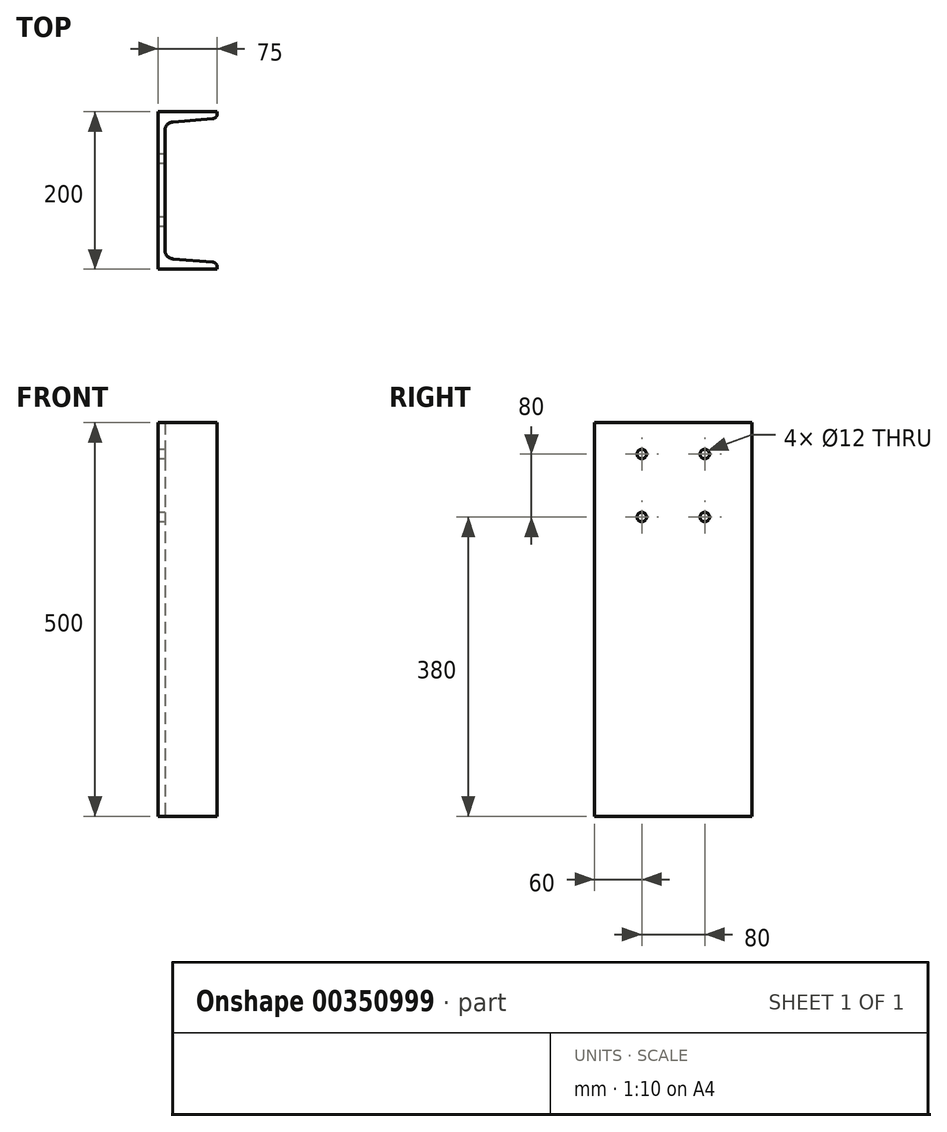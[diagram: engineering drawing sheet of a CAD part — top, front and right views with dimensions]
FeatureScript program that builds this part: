
annotation { "Feature Type Name" : "Feature", "Feature Type Description" : "" }
export const myFeature = defineFeature(function(context is Context, id is Id, definition is map)
    precondition{}
    {
        {
            var Q0;
            Q0=qCreatedBy(makeId("Top.planeOp"),FACE);
            var sketch = newSketch(context, id + "F0", { "sketchPlane" : qUnion([Q0])});
            skLineSegment(sketch, "E0", {"start": v(0, 0) * mm, "end": v(0, 100) * mm});
            skLineSegment(sketch, "E1", {"start": v(0, 0) * mm, "end": v(75, 0) * mm});
            skLineSegment(sketch, "E2.0", {"start": v(8.5, 24.44) * mm, "end": v(8.5, 100) * mm});
            skLineSegment(sketch, "E3", {"start": v(75, 0) * mm, "end": v(75, 2.5) * mm});
            skLineSegment(sketch, "E4", {"start": v(69.02, 8.98) * mm, "end": v(19.08, 12.97) * mm});
            skPoint(sketch, "E5.orphan", {"position": v(37.5, 11.5) * mm});
            skArc(sketch, "E6.filletArc", {"start": v(8.5, 24.44) * mm, "mid": v(11.55, 16.64) * mm, "end": v(19.08, 12.97) * mm});
            skPoint(sketch, "E7.visualSharp", {"position": v(75, 8.5) * mm});
            skArc(sketch, "E7.filletArc", {"start": v(75, 2.5) * mm, "mid": v(73.28, 6.9) * mm, "end": v(69.02, 8.98) * mm});
            skPoint(sketch, "E8.endSnap0", {"position": v(0, 100) * mm});
            skLineSegment(sketch, "E9.MirrorCS", {"start": v(75, 200) * mm, "end": v(75, 197.5) * mm});
            skArc(sketch, "E10.MirrorCS", {"start": v(75, 197.5) * mm, "mid": v(73.28, 193.1) * mm, "end": v(69.02, 191.02) * mm});
            skPoint(sketch, "E11.MirrorP", {"position": v(75, 191.5) * mm});
            skLineSegment(sketch, "E12.MirrorCS", {"start": v(69.02, 191.02) * mm, "end": v(19.08, 187.03) * mm});
            skLineSegment(sketch, "E13.MirrorCS", {"start": v(0, 200) * mm, "end": v(75, 200) * mm});
            skLineSegment(sketch, "E14.MirrorCS", {"start": v(8.5, 175.56) * mm, "end": v(8.5, 100) * mm});
            skArc(sketch, "E15.MirrorCS", {"start": v(8.5, 175.56) * mm, "mid": v(11.55, 183.36) * mm, "end": v(19.08, 187.03) * mm});
            skLineSegment(sketch, "E16.MirrorCS", {"start": v(0, 200) * mm, "end": v(0, 100) * mm});
            skPoint(sketch, "E17.MirrorP", {"position": v(37.5, 188.5) * mm});
            skSolve(sketch);
        }
        {
            var Q0;
            Q0=makeQuery(id+"F0.imprint","IMPRINT",FACE,{"disambiguationData":[TD([[makeQuery(id+"F0.imprint","IMPRINT",EDGE,{"derivedFrom":sQuery(id+"F0.wireOp",EDGE,"E0")}),-1.0]])]});
            extrude(context, id + "F1", {"entities" : qUnion([Q0]), "endBound" : BoundingType.SYMMETRIC, "depth" : 500 * mm});
        }
        {
            var Q0;
            Q0=makeQuery(id+"F1.opExtrude","SWEPT_FACE",FACE,{"disambiguationData":[OSD([sQuery(id+"F0.wireOp",EDGE,"E0"),sQuery(id+"F0.wireOp",EDGE,"E16.MirrorCS")])]});
            var sketch = newSketch(context, id + "F2", { "sketchPlane" : qUnion([Q0])});
            skLineSegment(sketch, "E18", {"start": v(18.26, 210) * mm, "end": v(-233.77, 210) * mm, "construction": true});
            skLineSegment(sketch, "E19", {"start": v(-60, -96.93) * mm, "end": v(-60, 240.61) * mm, "construction": true});
            skLineSegment(sketch, "E20", {"start": v(-100, 250) * mm, "end": v(-100, -139.95) * mm, "construction": true});
            skPoint(sketch, "E20.endSnap0", {"position": v(-100, 250) * mm});
            skLineSegment(sketch, "E21", {"start": v(-140, 228.97) * mm, "end": v(-140, -127.8) * mm, "construction": true});
            skLineSegment(sketch, "E22.0", {"start": v(18.26, 130) * mm, "end": v(-233.77, 130) * mm, "construction": true});
            skCircle(sketch, "E23", {"center": v(-60, 130) * mm, "radius": 6 * mm});
            skCircle(sketch, "E24", {"center": v(-140, 130) * mm, "radius": 6 * mm});
            skCircle(sketch, "E25", {"center": v(-60, 210) * mm, "radius": 6 * mm});
            skCircle(sketch, "E26", {"center": v(-140, 210) * mm, "radius": 6 * mm});
            skSolve(sketch);
        }
        {
            var Q0;
            Q0=makeQuery(id+"F2.imprint","IMPRINT",FACE,{"disambiguationData":[TD([[makeQuery(id+"F2.imprint","IMPRINT",EDGE,{"derivedFrom":sQuery(id+"F2.wireOp",EDGE,"E25")}),1.0]])]});
            var Q1;
            Q1=makeQuery(id+"F2.imprint","IMPRINT",FACE,{"disambiguationData":[TD([[makeQuery(id+"F2.imprint","IMPRINT",EDGE,{"derivedFrom":sQuery(id+"F2.wireOp",EDGE,"E26")}),1.0]])]});
            var Q2;
            Q2=makeQuery(id+"F2.imprint","IMPRINT",FACE,{"disambiguationData":[TD([[makeQuery(id+"F2.imprint","IMPRINT",EDGE,{"derivedFrom":sQuery(id+"F2.wireOp",EDGE,"E23")}),1.0]])]});
            var Q3;
            Q3=makeQuery(id+"F2.imprint","IMPRINT",FACE,{"disambiguationData":[TD([[makeQuery(id+"F2.imprint","IMPRINT",EDGE,{"derivedFrom":sQuery(id+"F2.wireOp",EDGE,"E24")}),1.0]])]});
            extrude(context, id + "F3", {"entities" : qUnion([Q0, Q1, Q2, Q3]), "operationType" : NewBodyOperationType.REMOVE, "endBound" : BoundingType.THROUGH_ALL, "oppositeDirection" : true, "depth" : 25 * mm});
        }
    });
